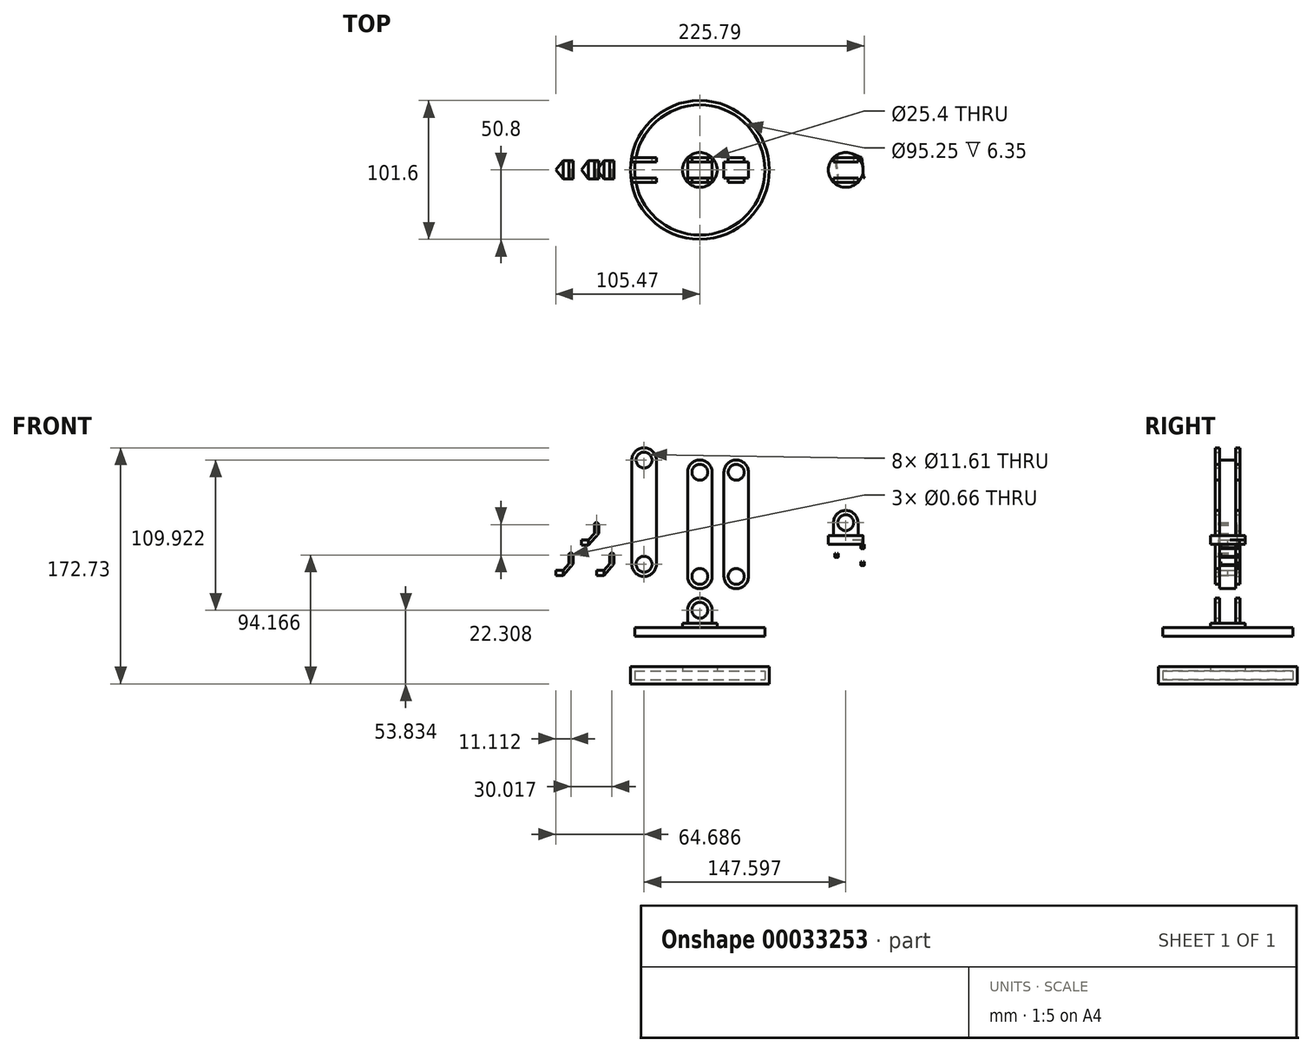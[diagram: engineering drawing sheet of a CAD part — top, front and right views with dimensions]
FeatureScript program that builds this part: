
annotation { "Feature Type Name" : "Feature", "Feature Type Description" : "" }
export const myFeature = defineFeature(function(context is Context, id is Id, definition is map)
    precondition{}
    {
        {
            var Q0;
            Q0=qCreatedBy(makeId("Front.planeOp"),FACE);
            var sketch = newSketch(context, id + "F0", { "sketchPlane" : qUnion([Q0])});
            skLineSegment(sketch, "E0", {"start": v(0, -146.74) * mm, "end": v(0, 149.22) * mm, "construction": true});
            skLineSegment(sketch, "E1.bottom", {"start": v(0, -76.61) * mm, "end": v(50.8, -76.61) * mm});
            skLineSegment(sketch, "E1.top", {"start": v(0, -63.91) * mm, "end": v(50.8, -63.91) * mm});
            skLineSegment(sketch, "E1.left", {"start": v(0, -76.61) * mm, "end": v(0, -63.91) * mm});
            skLineSegment(sketch, "E1.right", {"start": v(50.8, -76.61) * mm, "end": v(50.8, -63.91) * mm});
            skLineSegment(sketch, "E2.0", {"start": v(0, -73.44) * mm, "end": v(47.63, -73.44) * mm});
            skLineSegment(sketch, "E2.1", {"start": v(47.63, -73.44) * mm, "end": v(47.63, -67.09) * mm});
            skLineSegment(sketch, "E2.2", {"start": v(0, -67.09) * mm, "end": v(47.63, -67.09) * mm});
            skLineSegment(sketch, "E3", {"start": v(12.7, -67.09) * mm, "end": v(12.7, -63.91) * mm});
            skLineSegment(sketch, "E4.bottom", {"start": v(0, -45) * mm, "end": v(50.8, -45) * mm});
            skLineSegment(sketch, "E4.top", {"start": v(0, -32.3) * mm, "end": v(50.8, -32.3) * mm});
            skLineSegment(sketch, "E4.left", {"start": v(0, -45) * mm, "end": v(0, -32.3) * mm});
            skLineSegment(sketch, "E4.right", {"start": v(50.8, -45) * mm, "end": v(50.8, -32.3) * mm});
            skLineSegment(sketch, "E5.0", {"start": v(0, -41.83) * mm, "end": v(47.63, -41.83) * mm});
            skLineSegment(sketch, "E5.1", {"start": v(47.63, -41.83) * mm, "end": v(47.63, -35.48) * mm});
            skLineSegment(sketch, "E5.2", {"start": v(0, -35.48) * mm, "end": v(47.63, -35.48) * mm});
            skLineSegment(sketch, "E6", {"start": v(12.7, -35.48) * mm, "end": v(12.7, -32.3) * mm});
            skSolve(sketch);
        }
        {
            var Q0;
            {var subQ6=sQuery(id+"F0.wireOp",EDGE,"E1.bottom");Q0=makeQuery(id+"F0.imprint","IMPRINT",FACE,{"disambiguationData":[TD([[makeQuery(id+"F0.imprint","IMPRINT",EDGE,{"derivedFrom":subQ6}),1.0]])]});}
            var Q1;
            {var subQ5=sQuery(id+"F0.wireOp",EDGE,"E5.0");Q1=makeQuery(id+"F0.imprint","IMPRINT",FACE,{"disambiguationData":[TD([[makeQuery(id+"F0.imprint","IMPRINT",EDGE,{"derivedFrom":subQ5}),1.0]])]});}
            var Q2;
            {var subQ0=sQuery(id+"F0.wireOp",EDGE,"E6");Q2=makeQuery(id+"F0.imprint","IMPRINT",FACE,{"disambiguationData":[TD([[makeQuery(id+"F0.imprint","IMPRINT",EDGE,{"derivedFrom":subQ0}),1.0]])]});}
            var Q3;
            Q3=sQuery(id+"F0.wireOp",EDGE,"E0");
            revolve(context, id + "F1", {"entities" : qUnion([Q0, Q1, Q2]), "axis" : qUnion([Q3]), "revolveType" : RevolveType.FULL});
        }
        {
            var Q0;
            Q0=makeQuery(id+"F1.opRevolve","SWEPT_FACE",FACE,{"disambiguationData":[OSD([sQuery(id+"F0.wireOp",EDGE,"E4.top")])]});
            var sketch = newSketch(context, id + "F2", { "sketchPlane" : qUnion([Q0])});
            skLineSegment(sketch, "E7.rect.bottom", {"start": v(-8.98, 8.98) * mm, "end": v(8.98, 8.98) * mm});
            skLineSegment(sketch, "E7.rect.top", {"start": v(-8.98, -8.98) * mm, "end": v(8.98, -8.98) * mm});
            skLineSegment(sketch, "E7.rect.left", {"start": v(-8.98, 8.98) * mm, "end": v(-8.98, -8.98) * mm});
            skLineSegment(sketch, "E7.rect.right", {"start": v(8.98, 8.98) * mm, "end": v(8.98, -8.98) * mm});
            skPoint(sketch, "E7.rect.middle", {"position": v(0, 0) * mm});
            skSolve(sketch);
        }
        {
            var Q0;
            Q0=makeQuery(id+"F2.imprint","IMPRINT",FACE,{"disambiguationData":[TD([[makeQuery(id+"F2.imprint","IMPRINT",EDGE,{"derivedFrom":sQuery(id+"F2.wireOp",EDGE,"E7.rect.bottom")}),-1.0]])]});
            extrude(context, id + "F3", {"entities" : qUnion([Q0]), "operationType" : NewBodyOperationType.ADD, "depth" : 3.17 * mm});
        }
        {
            var Q0;
            Q0=makeQuery(id+"F3.opExtrude","CAP_FACE",FACE,{"disambiguationData":[OSD([sQuery(id+"F2.wireOp",EDGE,"E7.rect.bottom"),sQuery(id+"F2.wireOp",EDGE,"E7.rect.top"),sQuery(id+"F2.wireOp",EDGE,"E7.rect.left"),sQuery(id+"F2.wireOp",EDGE,"E7.rect.right")])],"isStart":false});
            var sketch = newSketch(context, id + "F4", { "sketchPlane" : qUnion([Q0])});
            skLineSegment(sketch, "E8.bottom", {"start": v(8.98, 8.98) * mm, "end": v(-8.98, 8.98) * mm});
            skLineSegment(sketch, "E8.top", {"start": v(8.98, 5.8) * mm, "end": v(-8.98, 5.8) * mm});
            skLineSegment(sketch, "E8.left", {"start": v(8.98, 8.98) * mm, "end": v(8.98, 5.8) * mm});
            skLineSegment(sketch, "E8.right", {"start": v(-8.98, 8.98) * mm, "end": v(-8.98, 5.8) * mm});
            skLineSegment(sketch, "E9.bottom", {"start": v(8.98, -8.98) * mm, "end": v(-8.98, -8.98) * mm});
            skLineSegment(sketch, "E9.top", {"start": v(8.98, -5.8) * mm, "end": v(-8.98, -5.8) * mm});
            skLineSegment(sketch, "E9.left", {"start": v(8.98, -8.98) * mm, "end": v(8.98, -5.8) * mm});
            skLineSegment(sketch, "E9.right", {"start": v(-8.98, -8.98) * mm, "end": v(-8.98, -5.8) * mm});
            skSolve(sketch);
        }
        {
            var Q0;
            Q0=makeQuery(id+"F4.imprint","IMPRINT",FACE,{"disambiguationData":[TD([[makeQuery(id+"F4.imprint","IMPRINT",EDGE,{"derivedFrom":sQuery(id+"F4.wireOp",EDGE,"E8.bottom")}),-1.0]])]});
            var Q1;
            Q1=makeQuery(id+"F4.imprint","IMPRINT",FACE,{"disambiguationData":[TD([[makeQuery(id+"F4.imprint","IMPRINT",EDGE,{"derivedFrom":sQuery(id+"F4.wireOp",EDGE,"E9.bottom")}),1.0]])]});
            extrude(context, id + "F5", {"entities" : qUnion([Q0, Q1]), "operationType" : NewBodyOperationType.ADD, "depth" : 6.35 * mm});
        }
        {
            var Q0;
            Q0=makeQuery(id+"F5.boolean.opBoolean","MERGE",FACE,{"derivedFrom":[makeQuery(id+"F3.opExtrude","SWEPT_FACE",FACE,{"disambiguationData":[OSD([sQuery(id+"F2.wireOp",EDGE,"E7.rect.bottom")])]}),makeQuery(id+"F5.opExtrude","SWEPT_FACE",FACE,{"disambiguationData":[OSD([sQuery(id+"F4.wireOp",EDGE,"E8.bottom")])]})]});
            var sketch = newSketch(context, id + "F6", { "sketchPlane" : qUnion([Q0])});
            skArc(sketch, "E10", {"start": v(8.98, -22.78) * mm, "mid": v(0, -13.8) * mm, "end": v(-8.98, -22.78) * mm});
            skCircle(sketch, "E11", {"center": v(0, -22.78) * mm, "radius": 5.8 * mm});
            skSolve(sketch);
        }
        {
            var Q0;
            Q0=makeQuery(id+"F6.imprint","IMPRINT",FACE,{"disambiguationData":[TD([[makeQuery(id+"F6.imprint","IMPRINT",EDGE,{"derivedFrom":sQuery(id+"F6.wireOp",EDGE,"E10")}),1.0]])]});
            extrude(context, id + "F7", {"entities" : qUnion([Q0]), "operationType" : NewBodyOperationType.ADD, "oppositeDirection" : true, "depth" : 3.17 * mm});
        }
        {
            var Q0;
            {var subQ0=makeQuery(id+"F5.opExtrude","CAP_EDGE",EDGE,{"disambiguationData":[OSD([sQuery(id+"F4.wireOp",EDGE,"E8.bottom")])],"isStart":false});var subQ1=sQuery(id+"F6.wireOp",EDGE,"E11");var subQ3=makeQuery(id+"F6.imprint","INTERSECT",VERTEX,{"disambiguationData":[OD(0.0)],"derivedFrom":[subQ0,subQ1]});Q0=makeQuery(id+"F6.imprint","IMPRINT",FACE,{"disambiguationData":[TD([[makeQuery(id+"F6.imprint","IMPRINT",EDGE,{"disambiguationData":[TD([[subQ3,-1.0]])],"derivedFrom":subQ1}),1.0]])]});}
            var Q1;
            {var subQ0=makeQuery(id+"F5.opExtrude","CAP_EDGE",EDGE,{"disambiguationData":[OSD([sQuery(id+"F4.wireOp",EDGE,"E8.bottom")])],"isStart":false});var subQ1=sQuery(id+"F6.wireOp",EDGE,"E11");var subQ3=makeQuery(id+"F6.imprint","INTERSECT",VERTEX,{"disambiguationData":[OD(0.0)],"derivedFrom":[subQ0,subQ1]});Q1=makeQuery(id+"F6.imprint","IMPRINT",FACE,{"disambiguationData":[TD([[makeQuery(id+"F6.imprint","IMPRINT",EDGE,{"disambiguationData":[TD([[subQ3,1.0]])],"derivedFrom":subQ1}),1.0]])]});}
            extrude(context, id + "F8", {"entities" : qUnion([Q0, Q1]), "operationType" : NewBodyOperationType.REMOVE, "oppositeDirection" : true, "depth" : 25.4 * mm});
        }
        {
            var Q0;
            Q0=makeQuery(id+"F5.boolean.opBoolean","MERGE",FACE,{"derivedFrom":[makeQuery(id+"F3.opExtrude","SWEPT_FACE",FACE,{"disambiguationData":[OSD([sQuery(id+"F2.wireOp",EDGE,"E7.rect.top")])]}),makeQuery(id+"F5.opExtrude","SWEPT_FACE",FACE,{"disambiguationData":[OSD([sQuery(id+"F4.wireOp",EDGE,"E9.bottom")])]})]});
            var sketch = newSketch(context, id + "F9", { "sketchPlane" : qUnion([Q0])});
            skArc(sketch, "E12", {"start": v(8.98, -22.78) * mm, "mid": v(0, -13.8) * mm, "end": v(-8.98, -22.78) * mm});
            skCircle(sketch, "E13", {"center": v(0, -22.78) * mm, "radius": 5.8 * mm});
            skSolve(sketch);
        }
        {
            var Q0;
            Q0=makeQuery(id+"F9.imprint","IMPRINT",FACE,{"disambiguationData":[TD([[makeQuery(id+"F9.imprint","IMPRINT",EDGE,{"derivedFrom":sQuery(id+"F9.wireOp",EDGE,"E12")}),1.0]])]});
            extrude(context, id + "F10", {"entities" : qUnion([Q0]), "operationType" : NewBodyOperationType.ADD, "oppositeDirection" : true, "depth" : 3.17 * mm});
        }
        {
            var Q0;
            Q0=makeQuery(id+"F3.opExtrude","CAP_FACE",FACE,{"disambiguationData":[OSD([sQuery(id+"F2.wireOp",EDGE,"E7.rect.bottom"),sQuery(id+"F2.wireOp",EDGE,"E7.rect.top"),sQuery(id+"F2.wireOp",EDGE,"E7.rect.left"),sQuery(id+"F2.wireOp",EDGE,"E7.rect.right")])],"isStart":false});
            extrude(context, id + "F11", {"entities" : qUnion([Q0]), "operationType" : NewBodyOperationType.REMOVE, "oppositeDirection" : true, "depth" : 3.17 * mm});
        }
        {
            var Q0;
            Q0=qCreatedBy(makeId("Front.planeOp"),FACE);
            var sketch = newSketch(context, id + "F12", { "sketchPlane" : qUnion([Q0])});
            skLineSegment(sketch, "E14.rect.bottom", {"start": v(8.98, 78.2) * mm, "end": v(-8.98, 78.2) * mm});
            skLineSegment(sketch, "E14.rect.top", {"start": v(8.98, 2) * mm, "end": v(-8.98, 2) * mm});
            skLineSegment(sketch, "E14.rect.left", {"start": v(8.98, 78.2) * mm, "end": v(8.98, 2) * mm});
            skLineSegment(sketch, "E14.rect.right", {"start": v(-8.98, 78.2) * mm, "end": v(-8.98, 2) * mm});
            skPoint(sketch, "E14.rect.middle", {"position": v(0, 40.1) * mm});
            skArc(sketch, "E15", {"start": v(-8.98, 2) * mm, "mid": v(0, -6.99) * mm, "end": v(8.98, 2) * mm});
            skArc(sketch, "E16", {"start": v(8.98, 78.2) * mm, "mid": v(0, 87.17) * mm, "end": v(-8.98, 78.2) * mm});
            skCircle(sketch, "E17", {"center": v(0, 78.2) * mm, "radius": 5.8 * mm});
            skCircle(sketch, "E18", {"center": v(0, 2) * mm, "radius": 5.8 * mm});
            skSolve(sketch);
        }
        {
            var Q0;
            {var subQ9=sQuery(id+"F12.wireOp",EDGE,"E14.rect.left");Q0=makeQuery(id+"F12.imprint","IMPRINT",FACE,{"disambiguationData":[TD([[makeQuery(id+"F12.imprint","IMPRINT",EDGE,{"derivedFrom":subQ9}),-1.0]])]});}
            var Q1;
            {var subQ4=sQuery(id+"F12.wireOp",EDGE,"E16");Q1=makeQuery(id+"F12.imprint","IMPRINT",FACE,{"disambiguationData":[TD([[makeQuery(id+"F12.imprint","IMPRINT",EDGE,{"derivedFrom":subQ4}),1.0]])]});}
            var Q2;
            {var subQ4=sQuery(id+"F12.wireOp",EDGE,"E15");Q2=makeQuery(id+"F12.imprint","IMPRINT",FACE,{"disambiguationData":[TD([[makeQuery(id+"F12.imprint","IMPRINT",EDGE,{"derivedFrom":subQ4}),1.0]])]});}
            extrude(context, id + "F13", {"entities" : qUnion([Q0, Q1, Q2]), "endBound" : BoundingType.SYMMETRIC, "depth" : 11.6 * mm});
        }
        {
            var Q0;
            {var subQ0=sQuery(id+"F12.wireOp",EDGE,"E18");var subQ1=sQuery(id+"F12.wireOp",EDGE,"E14.rect.top");var subQ3=makeQuery(id+"F12.imprint","INTERSECT",VERTEX,{"disambiguationData":[OD(0.0)],"derivedFrom":[subQ1,subQ0]});Q0=makeQuery(id+"F12.imprint","IMPRINT",FACE,{"disambiguationData":[TD([[makeQuery(id+"F12.imprint","IMPRINT",EDGE,{"disambiguationData":[TD([[subQ3,-1.0]])],"derivedFrom":subQ1}),-1.0]])]});}
            var Q1;
            {var subQ0=sQuery(id+"F12.wireOp",EDGE,"E18");var subQ1=sQuery(id+"F12.wireOp",EDGE,"E14.rect.top");var subQ3=makeQuery(id+"F12.imprint","INTERSECT",VERTEX,{"disambiguationData":[OD(0.0)],"derivedFrom":[subQ1,subQ0]});Q1=makeQuery(id+"F12.imprint","IMPRINT",FACE,{"disambiguationData":[TD([[makeQuery(id+"F12.imprint","IMPRINT",EDGE,{"disambiguationData":[TD([[subQ3,-1.0]])],"derivedFrom":subQ1}),1.0]])]});}
            var Q2;
            {var subQ0=sQuery(id+"F12.wireOp",EDGE,"E17");var subQ1=sQuery(id+"F12.wireOp",EDGE,"E14.rect.bottom");var subQ3=makeQuery(id+"F12.imprint","INTERSECT",VERTEX,{"disambiguationData":[OD(0.0)],"derivedFrom":[subQ1,subQ0]});Q2=makeQuery(id+"F12.imprint","IMPRINT",FACE,{"disambiguationData":[TD([[makeQuery(id+"F12.imprint","IMPRINT",EDGE,{"disambiguationData":[TD([[subQ3,-1.0]])],"derivedFrom":subQ1}),1.0]])]});}
            var Q3;
            {var subQ0=sQuery(id+"F12.wireOp",EDGE,"E17");var subQ1=sQuery(id+"F12.wireOp",EDGE,"E14.rect.bottom");var subQ3=makeQuery(id+"F12.imprint","INTERSECT",VERTEX,{"disambiguationData":[OD(0.0)],"derivedFrom":[subQ1,subQ0]});Q3=makeQuery(id+"F12.imprint","IMPRINT",FACE,{"disambiguationData":[TD([[makeQuery(id+"F12.imprint","IMPRINT",EDGE,{"disambiguationData":[TD([[subQ3,-1.0]])],"derivedFrom":subQ1}),-1.0]])]});}
            extrude(context, id + "F14", {"entities" : qUnion([Q0, Q1, Q2, Q3]), "operationType" : NewBodyOperationType.ADD, "endBound" : BoundingType.SYMMETRIC, "depth" : 17.96 * mm});
        }
        {
            var Q0;
            Q0=makeQuery(id+"F13.opExtrude","SWEPT_BODY",BODY,{"disambiguationData":[OSD([sQuery(id+"F12.wireOp",EDGE,"E14.rect.left"),sQuery(id+"F12.wireOp",EDGE,"E14.rect.right"),sQuery(id+"F12.wireOp",EDGE,"E15"),sQuery(id+"F12.wireOp",EDGE,"E16"),sQuery(id+"F12.wireOp",EDGE,"E17"),sQuery(id+"F12.wireOp",EDGE,"E18")])]});
            transform(context, id + "F15", {"entities" : qUnion([Q0]), "transformType" : TransformType.TRANSLATION_3D, "dx" : 26.6 * mm, "dy" : 0 * mm, "dz" : 0 * mm, "makeCopy" : true});
        }
        {
            var Q0;
            Q0=qCreatedBy(makeId("Front.planeOp"),FACE);
            var sketch = newSketch(context, id + "F16", { "sketchPlane" : qUnion([Q0])});
            skLineSegment(sketch, "E19.rect.bottom", {"start": v(-31.8, 87.15) * mm, "end": v(-49.76, 87.15) * mm});
            skLineSegment(sketch, "E19.rect.top", {"start": v(-31.8, 10.95) * mm, "end": v(-49.76, 10.95) * mm});
            skLineSegment(sketch, "E19.rect.left", {"start": v(-31.8, 87.15) * mm, "end": v(-31.8, 10.95) * mm});
            skLineSegment(sketch, "E19.rect.right", {"start": v(-49.76, 87.15) * mm, "end": v(-49.76, 10.95) * mm});
            skPoint(sketch, "E19.rect.middle", {"position": v(-40.78, 49.05) * mm});
            skArc(sketch, "E20", {"start": v(-49.76, 10.95) * mm, "mid": v(-40.78, 1.97) * mm, "end": v(-31.8, 10.95) * mm});
            skArc(sketch, "E21", {"start": v(-31.8, 87.15) * mm, "mid": v(-40.78, 96.12) * mm, "end": v(-49.76, 87.15) * mm});
            skCircle(sketch, "E22", {"center": v(-40.78, 87.15) * mm, "radius": 5.8 * mm});
            skCircle(sketch, "E23", {"center": v(-40.78, 10.95) * mm, "radius": 5.8 * mm});
            skSolve(sketch);
        }
        {
            var Q0;
            {var subQ5=sQuery(id+"F16.wireOp",EDGE,"E19.rect.left");Q0=makeQuery(id+"F16.imprint","IMPRINT",FACE,{"disambiguationData":[TD([[makeQuery(id+"F16.imprint","IMPRINT",EDGE,{"derivedFrom":subQ5}),-1.0]])]});}
            var Q1;
            {var subQ4=sQuery(id+"F16.wireOp",EDGE,"E20");Q1=makeQuery(id+"F16.imprint","IMPRINT",FACE,{"disambiguationData":[TD([[makeQuery(id+"F16.imprint","IMPRINT",EDGE,{"derivedFrom":subQ4}),1.0]])]});}
            var Q2;
            {var subQ4=sQuery(id+"F16.wireOp",EDGE,"E21");Q2=makeQuery(id+"F16.imprint","IMPRINT",FACE,{"disambiguationData":[TD([[makeQuery(id+"F16.imprint","IMPRINT",EDGE,{"derivedFrom":subQ4}),1.0]])]});}
            extrude(context, id + "F17", {"entities" : qUnion([Q0, Q1, Q2]), "endBound" : BoundingType.SYMMETRIC, "depth" : 17.96 * mm});
        }
        {
            var Q0;
            Q0=makeQuery(id+"F17.opExtrude","SWEPT_FACE",FACE,{"disambiguationData":[OSD([sQuery(id+"F16.wireOp",EDGE,"E19.rect.left")])]});
            var sketch = newSketch(context, id + "F18", { "sketchPlane" : qUnion([Q0])});
            skLineSegment(sketch, "E24.rect.bottom", {"start": v(5.8, 108.06) * mm, "end": v(-5.8, 108.06) * mm});
            skLineSegment(sketch, "E24.rect.top", {"start": v(5.8, -9.97) * mm, "end": v(-5.8, -9.97) * mm});
            skLineSegment(sketch, "E24.rect.left", {"start": v(5.8, 108.06) * mm, "end": v(5.8, -9.97) * mm});
            skLineSegment(sketch, "E24.rect.right", {"start": v(-5.8, 108.06) * mm, "end": v(-5.8, -9.97) * mm});
            skPoint(sketch, "E24.rect.middle", {"position": v(0, 49.05) * mm});
            skPoint(sketch, "E24.rect.middle.positionSnap0", {"position": v(-8.98, 49.05) * mm});
            skPoint(sketch, "E24.rect.centerSnap0", {"position": v(-8.98, 49.05) * mm});
            skSolve(sketch);
        }
        {
            var Q0;
            {var subQ5=sQuery(id+"F18.wireOp",EDGE,"E24.rect.bottom");Q0=makeQuery(id+"F18.imprint","IMPRINT",FACE,{"disambiguationData":[TD([[makeQuery(id+"F18.imprint","IMPRINT",EDGE,{"derivedFrom":subQ5}),1.0]])]});}
            var Q1;
            {var subQ0=sQuery(id+"F16.wireOp",EDGE,"E19.rect.left");var subQ4=sQuery(id+"F18.wireOp",EDGE,"E24.rect.left");var subQ6=makeQuery(id+"F17.opExtrude","SWEPT_EDGE",EDGE,{"disambiguationData":[OSD([sQuery(id+"F16.wireOp",EDGE,"E19.rect.bottom"),subQ0,sQuery(id+"F16.wireOp",EDGE,"E21")])]});var subQ8=makeQuery(id+"F18.imprint","INTERSECT",VERTEX,{"derivedFrom":[subQ6,subQ4]});Q1=makeQuery(id+"F18.imprint","IMPRINT",FACE,{"disambiguationData":[TD([[makeQuery(id+"F18.imprint","IMPRINT",EDGE,{"disambiguationData":[TD([[subQ8,-1.0]])],"derivedFrom":subQ4}),-1.0]])]});}
            var Q2;
            {var subQ5=sQuery(id+"F18.wireOp",EDGE,"E24.rect.top");Q2=makeQuery(id+"F18.imprint","IMPRINT",FACE,{"disambiguationData":[TD([[makeQuery(id+"F18.imprint","IMPRINT",EDGE,{"derivedFrom":subQ5}),-1.0]])]});}
            extrude(context, id + "F19", {"entities" : qUnion([Q0, Q1, Q2]), "operationType" : NewBodyOperationType.REMOVE, "oppositeDirection" : true, "depth" : 25.4 * mm});
        }
        {
            var Q0;
            Q0=makeQuery(id+"F1.opRevolve","SWEPT_BODY",BODY,{"disambiguationData":[OSD([sQuery(id+"F0.wireOp",EDGE,"E4.top"),sQuery(id+"F0.wireOp",EDGE,"E4.left"),sQuery(id+"F0.wireOp",EDGE,"E5.0"),sQuery(id+"F0.wireOp",EDGE,"E5.1"),sQuery(id+"F0.wireOp",EDGE,"E5.2"),sQuery(id+"F0.wireOp",EDGE,"E6")])]});
            var Q1;
            Q1=makeQuery(id+"F7.opExtrude","SWEPT_BODY",BODY,{"disambiguationData":[OSD([sQuery(id+"F4.wireOp",EDGE,"E8.bottom"),sQuery(id+"F6.wireOp",EDGE,"E10"),sQuery(id+"F6.wireOp",EDGE,"E11")])]});
            transform(context, id + "F20", {"entities" : qUnion([Q0, Q1]), "transformType" : TransformType.TRANSLATION_3D, "dx" : 106.81 * mm, "dy" : 0 * mm, "dz" : 64.05 * mm, "makeCopy" : true});
        }
        {
            var Q0;
            Q0=makeQuery(id+"F20.opPattern","COPY",FACE,{"derivedFrom":makeQuery(id+"F1.opRevolve","SWEPT_FACE",FACE,{"disambiguationData":[OSD([sQuery(id+"F0.wireOp",EDGE,"E5.0")])]}),"instanceName":"1"});
            extrude(context, id + "F21", {"entities" : qUnion([Q0]), "operationType" : NewBodyOperationType.REMOVE, "oppositeDirection" : true, "depth" : 6.35 * mm});
        }
        {
            var Q0;
            Q0=makeQuery(id+"F21.boolean.opBoolean","COPY",FACE,{"derivedFrom":makeQuery(id+"F21.opExtrude","CAP_FACE",FACE,{"disambiguationData":[OSD([sQuery(id+"F0.wireOp",EDGE,"E5.0")])],"isStart":false})});
            var sketch = newSketch(context, id + "F22", { "sketchPlane" : qUnion([Q0])});
            skCircle(sketch, "E25", {"center": v(106.81, 0) * mm, "radius": 12.7 * mm});
            skPoint(sketch, "E25.first.point", {"position": v(108, -12.64) * mm});
            skPoint(sketch, "E25.second.point", {"position": v(110.56, 12.13) * mm});
            skPoint(sketch, "E25.third.point", {"position": v(94.67, -3.71) * mm});
            skCircle(sketch, "E26.cCircle", {"center": v(106.81, 0) * mm, "radius": 12.7 * mm, "construction": true});
            skLineSegment(sketch, "E26.0", {"start": v(93.3, -5.71) * mm, "end": v(95.11, 8.84) * mm});
            skLineSegment(sketch, "E26.1", {"start": v(95.11, 8.84) * mm, "end": v(108.62, 14.55) * mm});
            skLineSegment(sketch, "E26.2", {"start": v(108.62, 14.55) * mm, "end": v(120.32, 5.71) * mm});
            skLineSegment(sketch, "E26.3", {"start": v(120.32, 5.71) * mm, "end": v(118.51, -8.84) * mm});
            skLineSegment(sketch, "E26.4", {"start": v(118.51, -8.84) * mm, "end": v(105, -14.55) * mm});
            skLineSegment(sketch, "E26.5", {"start": v(105, -14.55) * mm, "end": v(93.3, -5.71) * mm});
            skPoint(sketch, "E26.0.midPoint", {"position": v(94.2, 1.56) * mm});
            skPoint(sketch, "E27", {"position": v(99.16, -10.13) * mm});
            skSolve(sketch);
        }
        {
            var Q0;
            {var subQ0=sQuery(id+"F22.wireOp",EDGE,"E26.4");var subQ1=sQuery(id+"F22.wireOp",EDGE,"E25");var subQ2=makeQuery(id+"F22.imprint","INTERSECT",VERTEX,{"derivedFrom":[subQ1,subQ0]});Q0=makeQuery(id+"F22.imprint","IMPRINT",FACE,{"disambiguationData":[TD([[makeQuery(id+"F22.imprint","IMPRINT",EDGE,{"disambiguationData":[TD([[subQ2,-1.0]])],"derivedFrom":subQ1}),-1.0]])]});}
            var Q1;
            {var subQ1=sQuery(id+"F22.wireOp",EDGE,"E25");var subQ3=sQuery(id+"F22.wireOp",EDGE,"E26.4");var subQ5=makeQuery(id+"F22.imprint","INTERSECT",VERTEX,{"derivedFrom":[subQ1,subQ3]});Q1=makeQuery(id+"F22.imprint","IMPRINT",FACE,{"disambiguationData":[TD([[makeQuery(id+"F22.imprint","IMPRINT",EDGE,{"disambiguationData":[TD([[subQ5,1.0]])],"derivedFrom":subQ1}),-1.0]])]});}
            var Q2;
            {var subQ0=sQuery(id+"F22.wireOp",EDGE,"E26.5");var subQ1=sQuery(id+"F22.wireOp",EDGE,"E25");var subQ2=makeQuery(id+"F22.imprint","INTERSECT",VERTEX,{"derivedFrom":[subQ1,subQ0]});Q2=makeQuery(id+"F22.imprint","IMPRINT",FACE,{"disambiguationData":[TD([[makeQuery(id+"F22.imprint","IMPRINT",EDGE,{"disambiguationData":[TD([[subQ2,1.0]])],"derivedFrom":subQ1}),-1.0]])]});}
            var Q3;
            {var subQ0=sQuery(id+"F22.wireOp",EDGE,"E26.1");var subQ1=sQuery(id+"F22.wireOp",EDGE,"E25");var subQ2=makeQuery(id+"F22.imprint","INTERSECT",VERTEX,{"derivedFrom":[subQ1,subQ0]});Q3=makeQuery(id+"F22.imprint","IMPRINT",FACE,{"disambiguationData":[TD([[makeQuery(id+"F22.imprint","IMPRINT",EDGE,{"disambiguationData":[TD([[subQ2,-1.0]])],"derivedFrom":subQ1}),-1.0]])]});}
            var Q4;
            {var subQ0=sQuery(id+"F22.wireOp",EDGE,"E26.2");var subQ1=sQuery(id+"F22.wireOp",EDGE,"E25");var subQ2=makeQuery(id+"F22.imprint","INTERSECT",VERTEX,{"derivedFrom":[subQ1,subQ0]});Q4=makeQuery(id+"F22.imprint","IMPRINT",FACE,{"disambiguationData":[TD([[makeQuery(id+"F22.imprint","IMPRINT",EDGE,{"disambiguationData":[TD([[subQ2,-1.0]])],"derivedFrom":subQ1}),-1.0]])]});}
            var Q5;
            {var subQ1=sQuery(id+"F22.wireOp",EDGE,"E25");var subQ3=sQuery(id+"F22.wireOp",EDGE,"E26.3");var subQ5=makeQuery(id+"F22.imprint","INTERSECT",VERTEX,{"derivedFrom":[subQ1,subQ3]});Q5=makeQuery(id+"F22.imprint","IMPRINT",FACE,{"disambiguationData":[TD([[makeQuery(id+"F22.imprint","IMPRINT",EDGE,{"disambiguationData":[TD([[subQ5,-1.0]])],"derivedFrom":subQ1}),-1.0]])]});}
            var Q6;
            {var subQ0=sQuery(id+"F22.wireOp",EDGE,"E25");var subQ6=makeQuery(id+"F22.imprint","INTERSECT",VERTEX,{"derivedFrom":[subQ0,sQuery(id+"F22.wireOp",EDGE,"E26.4")]});Q6=makeQuery(id+"F22.imprint","IMPRINT",FACE,{"disambiguationData":[TD([[makeQuery(id+"F22.imprint","IMPRINT",EDGE,{"disambiguationData":[TD([[subQ6,1.0]])],"derivedFrom":subQ0}),1.0]])]});}
            extrude(context, id + "F23", {"entities" : qUnion([Q0, Q1, Q2, Q3, Q4, Q5, Q6]), "operationType" : NewBodyOperationType.ADD, "depth" : 3.17 * mm});
        }
        {
            var Q0;
            Q0=makeQuery(id+"F23.opExtrude","SWEPT_FACE",FACE,{"disambiguationData":[OSD([sQuery(id+"F22.wireOp",EDGE,"E26.3")])]});
            var sketch = newSketch(context, id + "F24", { "sketchPlane" : qUnion([Q0])});
            skLineSegment(sketch, "E28.bottom", {"start": v(-20.48, 25.4) * mm, "end": v(-5.81, 25.4) * mm});
            skLineSegment(sketch, "E28.top", {"start": v(-20.48, 22.4) * mm, "end": v(-5.81, 22.4) * mm});
            skLineSegment(sketch, "E28.left", {"start": v(-20.48, 25.4) * mm, "end": v(-20.48, 22.4) * mm});
            skLineSegment(sketch, "E28.right", {"start": v(-5.81, 25.4) * mm, "end": v(-5.81, 22.4) * mm});
            skLineSegment(sketch, "E29.0", {"start": v(-6.45, 25.4) * mm, "end": v(-6.45, 23.04) * mm});
            skLineSegment(sketch, "E29.1", {"start": v(-19.84, 23.04) * mm, "end": v(-6.45, 23.04) * mm});
            skLineSegment(sketch, "E29.2", {"start": v(-19.84, 25.4) * mm, "end": v(-19.84, 23.04) * mm});
            skSolve(sketch);
        }
        {
            var Q0;
            Q0=makeQuery(id+"F24.imprint","IMPRINT",FACE,{"disambiguationData":[TD([[makeQuery(id+"F24.imprint","IMPRINT",EDGE,{"derivedFrom":sQuery(id+"F24.wireOp",EDGE,"E28.top")}),1.0]])]});
            extrude(context, id + "F25", {"entities" : qUnion([Q0]), "oppositeDirection" : true, "depth" : 0.64 * mm});
        }
        {
            var Q0;
            Q0=makeQuery(id+"F25.opExtrude","CAP_EDGE",EDGE,{"disambiguationData":[OSD([sQuery(id+"F24.wireOp",EDGE,"E28.top")])],"isStart":true});
            var Q1;
            Q1=makeQuery(id+"F25.opExtrude","CAP_EDGE",EDGE,{"disambiguationData":[OSD([sQuery(id+"F24.wireOp",EDGE,"E29.1")])],"isStart":false});
            var Q2;
            Q2=makeQuery(id+"F25.opExtrude","CAP_EDGE",EDGE,{"disambiguationData":[OSD([sQuery(id+"F24.wireOp",EDGE,"E29.1")])],"isStart":true});
            var Q3;
            Q3=makeQuery(id+"F25.opExtrude","CAP_EDGE",EDGE,{"disambiguationData":[OSD([sQuery(id+"F24.wireOp",EDGE,"E28.top")])],"isStart":false});
            fillet(context, id + "F26", {"entities" : qUnion([Q0, Q1, Q2, Q3]), "radius" : 0.32 * mm, "tangentPropagation" : true, "allowEdgeOverflow" : false});
        }
        {
            var Q0;
            Q0=makeQuery(id+"F25.opExtrude","SWEPT_BODY",BODY,{"disambiguationData":[OSD([sQuery(id+"F24.wireOp",EDGE,"E28.bottom"),sQuery(id+"F24.wireOp",EDGE,"E28.top"),sQuery(id+"F24.wireOp",EDGE,"E28.left"),sQuery(id+"F24.wireOp",EDGE,"E28.right"),sQuery(id+"F24.wireOp",EDGE,"E29.0"),sQuery(id+"F24.wireOp",EDGE,"E29.1"),sQuery(id+"F24.wireOp",EDGE,"E29.2")])]});
            transform(context, id + "F27", {"entities" : qUnion([Q0]), "transformType" : TransformType.TRANSLATION_3D, "dx" : -19.06 * mm, "dy" : 0 * mm, "dz" : -6.5 * mm, "makeCopy" : true});
        }
        {
            var Q0;
            Q0=makeQuery(id+"F25.opExtrude","SWEPT_BODY",BODY,{"disambiguationData":[OSD([sQuery(id+"F24.wireOp",EDGE,"E28.bottom"),sQuery(id+"F24.wireOp",EDGE,"E28.top"),sQuery(id+"F24.wireOp",EDGE,"E28.left"),sQuery(id+"F24.wireOp",EDGE,"E28.right"),sQuery(id+"F24.wireOp",EDGE,"E29.0"),sQuery(id+"F24.wireOp",EDGE,"E29.1"),sQuery(id+"F24.wireOp",EDGE,"E29.2")])]});
            transform(context, id + "F28", {"entities" : qUnion([Q0]), "transformType" : TransformType.TRANSLATION_3D, "dx" : 0 * mm, "dy" : 0 * mm, "dz" : -12.47 * mm, "makeCopy" : true});
        }
        {
            var Q0;
            Q0=qCreatedBy(makeId("Front.planeOp"),FACE);
            var sketch = newSketch(context, id + "F29", { "sketchPlane" : qUnion([Q0])});
            skLineSegment(sketch, "E30.bottom", {"start": v(-95.95, 17.56) * mm, "end": v(-92.77, 17.56) * mm});
            skLineSegment(sketch, "E30.top", {"start": v(-95.95, 11.2) * mm, "end": v(-92.77, 11.2) * mm});
            skLineSegment(sketch, "E30.left", {"start": v(-95.95, 17.56) * mm, "end": v(-95.95, 11.2) * mm});
            skLineSegment(sketch, "E30.right", {"start": v(-92.77, 17.56) * mm, "end": v(-92.77, 11.2) * mm});
            skLineSegment(sketch, "E31", {"start": v(-92.77, 11.2) * mm, "end": v(-100.07, 2.66) * mm});
            skLineSegment(sketch, "E32", {"start": v(-95.95, 11.2) * mm, "end": v(-100.07, 6.38) * mm});
            skArc(sketch, "E33", {"start": v(-92.77, 17.56) * mm, "mid": v(-94.36, 19.14) * mm, "end": v(-95.95, 17.56) * mm});
            skCircle(sketch, "E34", {"center": v(-94.36, 17.56) * mm, "radius": 0.33 * mm});
            skLineSegment(sketch, "E35", {"start": v(-100.07, 6.38) * mm, "end": v(-100.07, 2.66) * mm});
            skLineSegment(sketch, "E36", {"start": v(-100.07, 2.66) * mm, "end": v(-92.77, 2.66) * mm});
            skLineSegment(sketch, "E37", {"start": v(-92.77, 2.66) * mm, "end": v(-92.77, 11.2) * mm});
            skLineSegment(sketch, "E38.bottom", {"start": v(-100.07, 2.66) * mm, "end": v(-105.47, 2.66) * mm});
            skLineSegment(sketch, "E38.top", {"start": v(-100.07, 6.38) * mm, "end": v(-105.47, 6.38) * mm});
            skLineSegment(sketch, "E38.left", {"start": v(-100.07, 2.66) * mm, "end": v(-100.07, 6.38) * mm});
            skLineSegment(sketch, "E38.right", {"start": v(-105.47, 2.66) * mm, "end": v(-105.47, 6.38) * mm});
            skSolve(sketch);
        }
        {
            var Q0;
            Q0=makeQuery(id+"F29.imprint","IMPRINT",FACE,{"disambiguationData":[TD([[makeQuery(id+"F29.imprint","IMPRINT",EDGE,{"derivedFrom":sQuery(id+"F29.wireOp",EDGE,"E30.top")}),1.0]])]});
            var Q1;
            {var subQ4=sQuery(id+"F29.wireOp",EDGE,"E33");Q1=makeQuery(id+"F29.imprint","IMPRINT",FACE,{"disambiguationData":[TD([[makeQuery(id+"F29.imprint","IMPRINT",EDGE,{"derivedFrom":subQ4}),1.0]])]});}
            var Q2;
            Q2=makeQuery(id+"F29.imprint","IMPRINT",FACE,{"disambiguationData":[TD([[makeQuery(id+"F29.imprint","IMPRINT",EDGE,{"derivedFrom":sQuery(id+"F29.wireOp",EDGE,"E30.top")}),-1.0]])]});
            var Q3;
            Q3=makeQuery(id+"F29.imprint","IMPRINT",FACE,{"disambiguationData":[TD([[makeQuery(id+"F29.imprint","IMPRINT",EDGE,{"derivedFrom":sQuery(id+"F29.wireOp",EDGE,"E38.bottom")}),-1.0]])]});
            extrude(context, id + "F30", {"entities" : qUnion([Q0, Q1, Q2, Q3]), "endBound" : BoundingType.SYMMETRIC, "depth" : 13.4 * mm});
        }
        {
            var Q0;
            Q0=makeQuery(id+"F30.opExtrude","SWEPT_FACE",FACE,{"disambiguationData":[OSD([sQuery(id+"F29.wireOp",EDGE,"E38.top")])]});
            var sketch = newSketch(context, id + "F31", { "sketchPlane" : qUnion([Q0])});
            skLineSegment(sketch, "E39", {"start": v(-100.07, -6.7) * mm, "end": v(-105.47, 0) * mm});
            skLineSegment(sketch, "E40", {"start": v(-105.47, 0) * mm, "end": v(-100.07, 6.7) * mm});
            skSolve(sketch);
        }
        {
            var Q0;
            {var subQ2=sQuery(id+"F31.wireOp",EDGE,"E39");Q0=makeQuery(id+"F31.imprint","IMPRINT",FACE,{"disambiguationData":[TD([[makeQuery(id+"F31.imprint","IMPRINT",EDGE,{"derivedFrom":subQ2}),1.0]])]});}
            var Q1;
            {var subQ2=sQuery(id+"F31.wireOp",EDGE,"E40");Q1=makeQuery(id+"F31.imprint","IMPRINT",FACE,{"disambiguationData":[TD([[makeQuery(id+"F31.imprint","IMPRINT",EDGE,{"derivedFrom":subQ2}),1.0]])]});}
            extrude(context, id + "F32", {"entities" : qUnion([Q0, Q1]), "operationType" : NewBodyOperationType.REMOVE, "oppositeDirection" : true, "depth" : 25.4 * mm});
        }
        {
            var Q0;
            Q0=makeQuery(id+"F30.opExtrude","SWEPT_BODY",BODY,{"disambiguationData":[OSD([sQuery(id+"F29.wireOp",EDGE,"E30.left"),sQuery(id+"F29.wireOp",EDGE,"E30.right"),sQuery(id+"F29.wireOp",EDGE,"E31"),sQuery(id+"F29.wireOp",EDGE,"E32"),sQuery(id+"F29.wireOp",EDGE,"E33"),sQuery(id+"F29.wireOp",EDGE,"E34"),sQuery(id+"F29.wireOp",EDGE,"E38.bottom"),sQuery(id+"F29.wireOp",EDGE,"E38.top"),sQuery(id+"F29.wireOp",EDGE,"E38.right")])]});
            transform(context, id + "F33", {"entities" : qUnion([Q0]), "transformType" : TransformType.TRANSLATION_3D, "dx" : 30.02 * mm, "dy" : 0 * mm, "dz" : 0 * mm, "makeCopy" : true});
        }
        {
            var Q0;
            Q0=makeQuery(id+"F30.opExtrude","SWEPT_BODY",BODY,{"disambiguationData":[OSD([sQuery(id+"F29.wireOp",EDGE,"E30.left"),sQuery(id+"F29.wireOp",EDGE,"E30.right"),sQuery(id+"F29.wireOp",EDGE,"E31"),sQuery(id+"F29.wireOp",EDGE,"E32"),sQuery(id+"F29.wireOp",EDGE,"E33"),sQuery(id+"F29.wireOp",EDGE,"E34"),sQuery(id+"F29.wireOp",EDGE,"E38.bottom"),sQuery(id+"F29.wireOp",EDGE,"E38.top"),sQuery(id+"F29.wireOp",EDGE,"E38.right")])]});
            transform(context, id + "F34", {"entities" : qUnion([Q0]), "transformType" : TransformType.TRANSLATION_3D, "dx" : 18.7 * mm, "dy" : 0 * mm, "dz" : 22.3 * mm, "makeCopy" : true});
        }
    });
